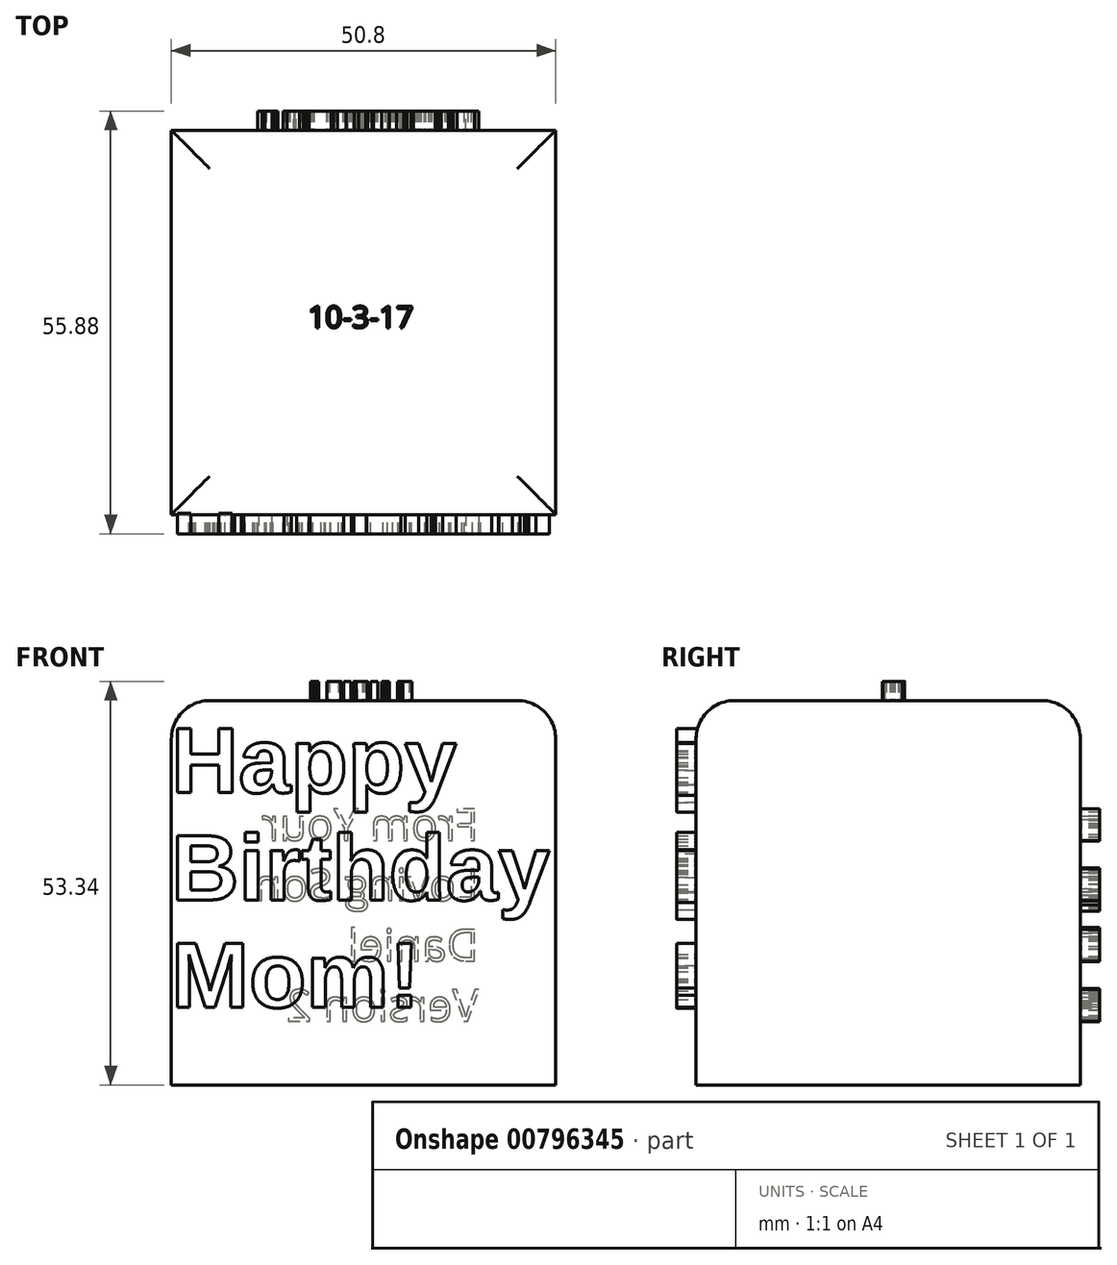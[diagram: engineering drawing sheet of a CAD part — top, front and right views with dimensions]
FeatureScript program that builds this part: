
annotation { "Feature Type Name" : "Feature", "Feature Type Description" : "" }
export const myFeature = defineFeature(function(context is Context, id is Id, definition is map)
    precondition{}
    {
        {
            var Q0;
            Q0=qCreatedBy(makeId("Top.planeOp"),FACE);
            var sketch = newSketch(context, id + "F0", { "sketchPlane" : qUnion([Q0])});
            skLineSegment(sketch, "E0.bottom", {"start": v(-147.56, -16.55) * mm, "end": v(-96.76, -16.55) * mm});
            skLineSegment(sketch, "E0.top", {"start": v(-147.56, -67.35) * mm, "end": v(-96.76, -67.35) * mm});
            skLineSegment(sketch, "E0.left", {"start": v(-147.56, -16.55) * mm, "end": v(-147.56, -67.35) * mm});
            skLineSegment(sketch, "E0.right", {"start": v(-96.76, -16.55) * mm, "end": v(-96.76, -67.35) * mm});
            skSolve(sketch);
        }
        {
            var Q0;
            Q0=makeQuery(id+"F0.imprint","IMPRINT",FACE,{"disambiguationData":[TD([[makeQuery(id+"F0.imprint","IMPRINT",EDGE,{"derivedFrom":sQuery(id+"F0.wireOp",EDGE,"E0.bottom")}),-1.0]])]});
            extrude(context, id + "F1", {"entities" : qUnion([Q0]), "depth" : 50.8 * mm, "offsetDistance" : 25.4 * mm});
        }
        {
            var Q0;
            Q0=makeQuery(id+"F1.opExtrude","SWEPT_FACE",FACE,{"disambiguationData":[OSD([sQuery(id+"F0.wireOp",EDGE,"E0.top")])]});
            var sketch = newSketch(context, id + "F2", { "sketchPlane" : qUnion([Q0])});
            skText(sketch, "E1", { "text": "Happy\nBirthday\nMom!", "fontName": "Arimo-Bold.ttf"});
            skPoint(sketch, "E2", {"position": v(-96.76, 25.4) * mm});
            const initialGuessF2  = {"E1": [-0.14756, 0.03862, 1, 0, 0.00888]};
            skSetInitialGuess(sketch, initialGuessF2);
            skSolve(sketch);
        }
        {
            var Q0;
            Q0 = qSketchRegion(id + "F2", true);
            extrude(context, id + "F3", {"entities" : qUnion([Q0]), "operationType" : NewBodyOperationType.ADD, "depth" : 2.54 * mm, "offsetDistance" : 25.4 * mm});
        }
        {
            var Q0;
            Q0=makeQuery(id+"F1.opExtrude","CAP_FACE",FACE,{"disambiguationData":[OSD([sQuery(id+"F0.wireOp",EDGE,"E0.bottom"),sQuery(id+"F0.wireOp",EDGE,"E0.top"),sQuery(id+"F0.wireOp",EDGE,"E0.left"),sQuery(id+"F0.wireOp",EDGE,"E0.right")])],"isStart":false});
            fillet(context, id + "F4", {"entities" : qUnion([Q0]), "radius" : 5.08 * mm, "tangentPropagation" : true, "allowEdgeOverflow" : false});
        }
        {
            var Q0;
            Q0=makeQuery(id+"F1.opExtrude","CAP_FACE",FACE,{"disambiguationData":[OSD([sQuery(id+"F0.wireOp",EDGE,"E0.bottom"),sQuery(id+"F0.wireOp",EDGE,"E0.top"),sQuery(id+"F0.wireOp",EDGE,"E0.left"),sQuery(id+"F0.wireOp",EDGE,"E0.right")])],"isStart":false});
            var sketch = newSketch(context, id + "F5", { "sketchPlane" : qUnion([Q0])});
            skText(sketch, "E3", { "text": "10-3-17", "fontName": "OpenSans-Regular.ttf"});
            const initialGuessF5  = {"E3": [-0.1295, -0.04266, 1, 0, 0.00286]};
            skSetInitialGuess(sketch, initialGuessF5);
            skSolve(sketch);
        }
        {
            var Q0;
            Q0 = qSketchRegion(id + "F5", true);
            extrude(context, id + "F6", {"entities" : qUnion([Q0]), "operationType" : NewBodyOperationType.ADD, "depth" : 2.54 * mm, "offsetDistance" : 25.4 * mm});
        }
        {
            var Q0;
            Q0=makeQuery(id+"F1.opExtrude","SWEPT_FACE",FACE,{"disambiguationData":[OSD([sQuery(id+"F0.wireOp",EDGE,"E0.bottom")])]});
            var sketch = newSketch(context, id + "F7", { "sketchPlane" : qUnion([Q0])});
            skText(sketch, "E4", { "text": "From Your \nLoving Son\nDaniel\nVersion 2", "fontName": "OpenSans-Regular.ttf"});
            const initialGuessF7  = {"E4": [0.10691, 0.03232, 1, 0, 0.00422]};
            skSetInitialGuess(sketch, initialGuessF7);
            skSolve(sketch);
        }
        {
            var Q0;
            Q0 = qSketchRegion(id + "F7", true);
            extrude(context, id + "F8", {"entities" : qUnion([Q0]), "operationType" : NewBodyOperationType.ADD, "depth" : 2.54 * mm, "offsetDistance" : 25.4 * mm});
        }
    });
